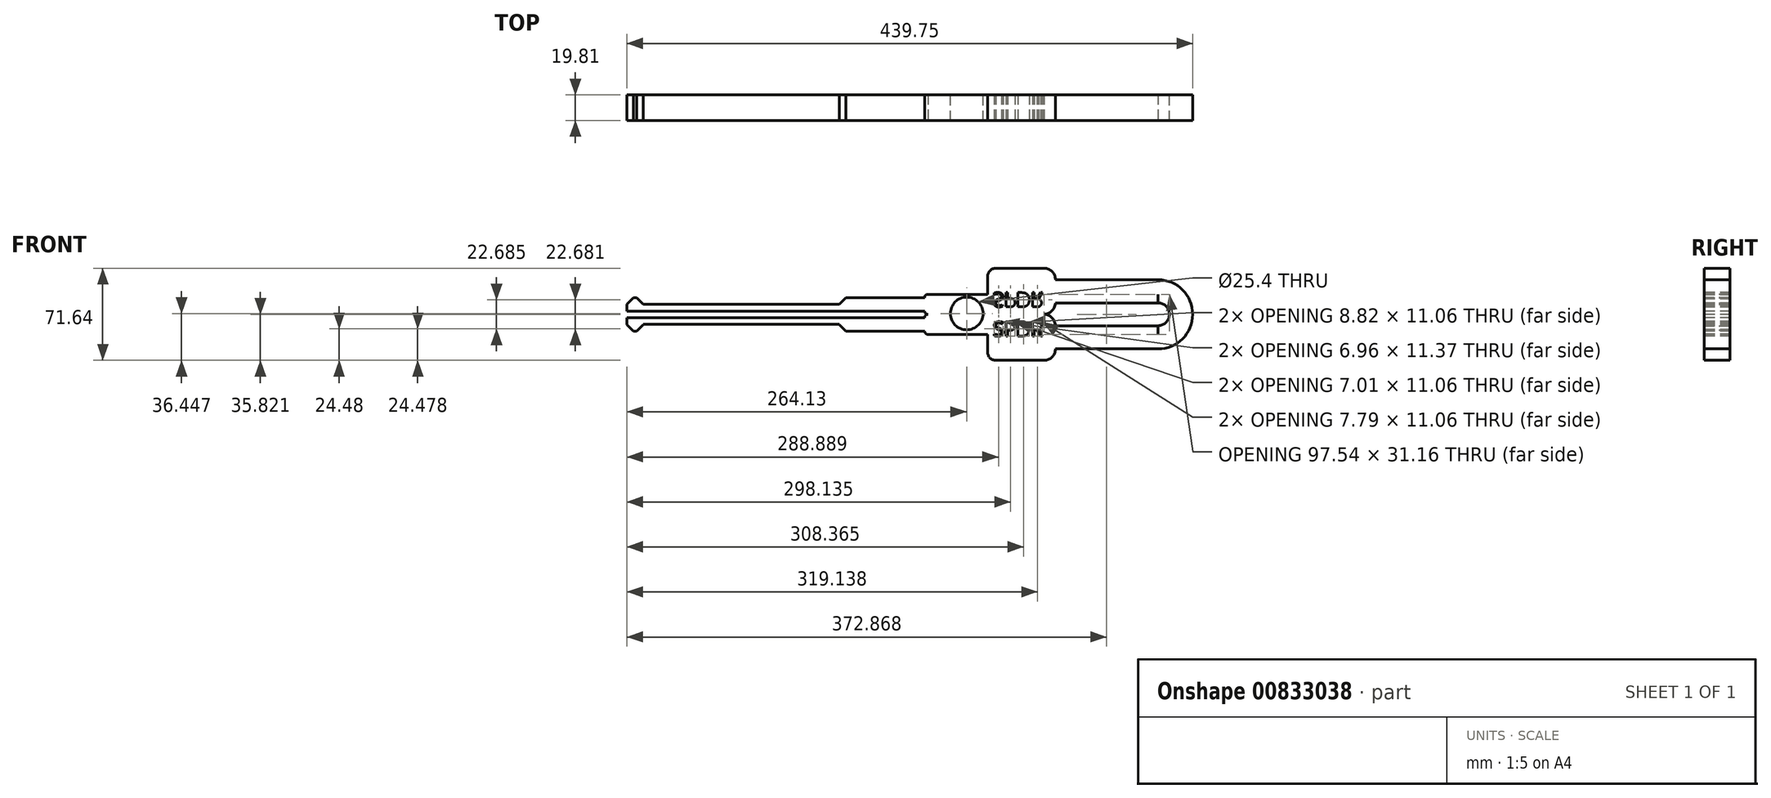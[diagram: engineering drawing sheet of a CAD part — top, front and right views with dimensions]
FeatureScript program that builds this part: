
annotation { "Feature Type Name" : "Feature", "Feature Type Description" : "" }
export const myFeature = defineFeature(function(context is Context, id is Id, definition is map)
    precondition{}
    {
        {
            var Q0;
            Q0=qCreatedBy(makeId("Front.planeOp"),FACE);
            var sketch = newSketch(context, id + "F0", { "sketchPlane" : qUnion([Q0])});
            skLineSegment(sketch, "E0.bottom", {"start": v(-48.26, 7.8) * mm, "end": v(41.91, 7.8) * mm});
            skLineSegment(sketch, "E0.top", {"start": v(-48.26, -7.8) * mm, "end": v(50.8, -7.8) * mm});
            skLineSegment(sketch, "E0.left", {"start": v(-50.8, 5.25) * mm, "end": v(-50.8, -5.25) * mm});
            skLineSegment(sketch, "E0.right", {"start": v(50.8, -1.1) * mm, "end": v(50.8, -7.8) * mm});
            skLineSegment(sketch, "E1.bottom", {"start": v(-1.8, -7.8) * mm, "end": v(50.88, -7.8) * mm});
            skLineSegment(sketch, "E1.top", {"start": v(4.55, -28.03) * mm, "end": v(42, -28.03) * mm});
            skLineSegment(sketch, "E1.left", {"start": v(-1.8, -7.8) * mm, "end": v(-1.8, -21.68) * mm});
            skLineSegment(sketch, "E1.right", {"start": v(50.88, -7.8) * mm, "end": v(50.88, -19.14) * mm});
            skPoint(sketch, "E2.visualSharp", {"position": v(-1.8, -28.03) * mm});
            skArc(sketch, "E2.filletArc", {"start": v(-1.8, -21.68) * mm, "mid": v(0.06, -26.17) * mm, "end": v(4.55, -28.03) * mm});
            skPoint(sketch, "E3.visualSharp", {"position": v(50.88, -28.03) * mm});
            skArc(sketch, "E3.filletArc", {"start": v(42, -28.03) * mm, "mid": v(48.28, -25.42) * mm, "end": v(50.88, -19.14) * mm});
            skPoint(sketch, "E4.visualSharp", {"position": v(50.8, 7.8) * mm});
            skArc(sketch, "E4.filletArc", {"start": v(50.8, -1.1) * mm, "mid": v(48.2, 5.19) * mm, "end": v(41.91, 7.8) * mm});
            skPoint(sketch, "E5.visualSharp", {"position": v(-50.8, -7.8) * mm});
            skArc(sketch, "E5.filletArc", {"start": v(-50.8, -5.25) * mm, "mid": v(-50.06, -7.05) * mm, "end": v(-48.26, -7.8) * mm});
            skPoint(sketch, "E6.visualSharp", {"position": v(-50.8, 7.8) * mm});
            skArc(sketch, "E6.filletArc", {"start": v(-48.26, 7.8) * mm, "mid": v(-50.06, 7.05) * mm, "end": v(-50.8, 5.25) * mm});
            skSolve(sketch);
        }
        {
            var Q0;
            Q0=makeQuery(id+"F0.imprint","IMPRINT",FACE,{"disambiguationData":[TD([[makeQuery(id+"F0.imprint","IMPRINT",EDGE,{"derivedFrom":sQuery(id+"F0.wireOp",EDGE,"E0.bottom")}),-1.0]])]});
            var Q1;
            Q1=makeQuery(id+"F0.imprint","IMPRINT",FACE,{"disambiguationData":[TD([[makeQuery(id+"F0.imprint","IMPRINT",EDGE,{"derivedFrom":sQuery(id+"F0.wireOp",EDGE,"E1.top")}),1.0]])]});
            extrude(context, id + "F1", {"entities" : qUnion([Q0, Q1]), "oppositeDirection" : true, "depth" : 19.8 * mm, "offsetDistance" : 25.4 * mm});
        }
        {
            var Q0;
            Q0=makeQuery(id+"F1.opExtrude","CAP_FACE",FACE,{"disambiguationData":[OSD([sQuery(id+"F0.wireOp",EDGE,"E0.bottom"),sQuery(id+"F0.wireOp",EDGE,"E0.top"),sQuery(id+"F0.wireOp",EDGE,"E0.left"),sQuery(id+"F0.wireOp",EDGE,"E0.right"),sQuery(id+"F0.wireOp",EDGE,"E1.bottom"),sQuery(id+"F0.wireOp",EDGE,"E1.top"),sQuery(id+"F0.wireOp",EDGE,"E1.left"),sQuery(id+"F0.wireOp",EDGE,"E1.right"),sQuery(id+"F0.wireOp",EDGE,"E2.filletArc"),sQuery(id+"F0.wireOp",EDGE,"E3.filletArc"),sQuery(id+"F0.wireOp",EDGE,"E4.filletArc"),sQuery(id+"F0.wireOp",EDGE,"E5.filletArc"),sQuery(id+"F0.wireOp",EDGE,"E6.filletArc")])],"isStart":true});
            var sketch = newSketch(context, id + "F2", { "sketchPlane" : qUnion([Q0])});
            skText(sketch, "E7", { "text": "SPDR", "fontName": "OpenSans-Regular.ttf"});
            const initialGuessF2  = {"E7": [0.00242, -0.00908, 1, 0, 0.01115]};
            skSetInitialGuess(sketch, initialGuessF2);
            skSolve(sketch);
        }
        {
            var Q0;
            Q0=makeQuery(id+"F2.imprint","IMPRINT",FACE,{"disambiguationData":[TD([[makeQuery(id+"F2.imprint","IMPRINT",EDGE,{"derivedFrom":sQuery(id+"F2.wireOp",EDGE,"E7.sketch_text.stroke-54")}),-1.0]])]});
            var Q1;
            Q1=makeQuery(id+"F2.imprint","IMPRINT",FACE,{"disambiguationData":[TD([[makeQuery(id+"F2.imprint","IMPRINT",EDGE,{"derivedFrom":sQuery(id+"F2.wireOp",EDGE,"E7.sketch_text.stroke-65")}),1.0]])]});
            var Q2;
            Q2=makeQuery(id+"F2.imprint","IMPRINT",FACE,{"disambiguationData":[TD([[makeQuery(id+"F2.imprint","IMPRINT",EDGE,{"derivedFrom":sQuery(id+"F2.wireOp",EDGE,"E7.sketch_text.stroke-40")}),-1.0]])]});
            var Q3;
            Q3=makeQuery(id+"F2.imprint","IMPRINT",FACE,{"disambiguationData":[TD([[makeQuery(id+"F2.imprint","IMPRINT",EDGE,{"derivedFrom":sQuery(id+"F2.wireOp",EDGE,"E7.sketch_text.stroke-47")}),1.0]])]});
            var Q4;
            Q4=makeQuery(id+"F2.imprint","IMPRINT",FACE,{"disambiguationData":[TD([[makeQuery(id+"F2.imprint","IMPRINT",EDGE,{"derivedFrom":sQuery(id+"F2.wireOp",EDGE,"E7.sketch_text.stroke-33")}),1.0]])]});
            var Q5;
            Q5=makeQuery(id+"F2.imprint","IMPRINT",FACE,{"disambiguationData":[TD([[makeQuery(id+"F2.imprint","IMPRINT",EDGE,{"derivedFrom":sQuery(id+"F2.wireOp",EDGE,"E7.sketch_text.stroke-25")}),-1.0]])]});
            var Q6;
            Q6=makeQuery(id+"F2.imprint","IMPRINT",FACE,{"disambiguationData":[TD([[makeQuery(id+"F2.imprint","IMPRINT",EDGE,{"derivedFrom":sQuery(id+"F2.wireOp",EDGE,"E7.sketch_text.stroke-0")}),-1.0]])]});
            extrude(context, id + "F3", {"entities" : qUnion([Q0, Q1, Q2, Q3, Q4, Q5, Q6]), "operationType" : NewBodyOperationType.REMOVE, "endBound" : BoundingType.THROUGH_ALL, "oppositeDirection" : true, "depth" : 44.45 * mm, "offsetDistance" : 25.4 * mm});
        }
        {
            var Q0;
            Q0=makeQuery(id+"F1.opExtrude","SWEPT_BODY",BODY,{"disambiguationData":[OSD([sQuery(id+"F0.wireOp",EDGE,"E0.bottom"),sQuery(id+"F0.wireOp",EDGE,"E0.top"),sQuery(id+"F0.wireOp",EDGE,"E0.left"),sQuery(id+"F0.wireOp",EDGE,"E0.right"),sQuery(id+"F0.wireOp",EDGE,"E1.bottom"),sQuery(id+"F0.wireOp",EDGE,"E1.top"),sQuery(id+"F0.wireOp",EDGE,"E1.left"),sQuery(id+"F0.wireOp",EDGE,"E1.right"),sQuery(id+"F0.wireOp",EDGE,"E2.filletArc"),sQuery(id+"F0.wireOp",EDGE,"E3.filletArc"),sQuery(id+"F0.wireOp",EDGE,"E4.filletArc"),sQuery(id+"F0.wireOp",EDGE,"E5.filletArc"),sQuery(id+"F0.wireOp",EDGE,"E6.filletArc")])]});
            var Q1;
            Q1=makeQuery(id+"F1.opExtrude","SWEPT_FACE",FACE,{"disambiguationData":[OSD([sQuery(id+"F0.wireOp",EDGE,"E0.bottom")])]});
            mirror(context, id + "F4", {"operationType" : NewBodyOperationType.ADD, "entities" : qUnion([Q0]), "mirrorPlane" : qUnion([Q1])});
        }
        {
            var Q0;
            Q0=makeQuery(id+"F4.opPattern","COPY",FACE,{"derivedFrom":makeQuery(id+"F1.opExtrude","SWEPT_FACE",FACE,{"disambiguationData":[OSD([sQuery(id+"F0.wireOp",EDGE,"E0.left")])]}),"instanceName":"1"});
            var Q1;
            Q1=makeQuery(id+"F1.opExtrude","SWEPT_FACE",FACE,{"disambiguationData":[OSD([sQuery(id+"F0.wireOp",EDGE,"E0.left")])]});
            extrude(context, id + "F5", {"entities" : qUnion([Q0, Q1]), "operationType" : NewBodyOperationType.ADD, "depth" : 231.4 * mm, "offsetDistance" : 25.4 * mm});
        }
        {
            var Q0;
            {var subQ0=sQuery(id+"F0.wireOp",EDGE,"E0.left");var subQ1=makeQuery(id+"F1.opExtrude","CAP_EDGE",EDGE,{"disambiguationData":[OSD([subQ0])],"isStart":true});var subQ2=makeQuery(id+"F1.opExtrude","CAP_FACE",FACE,{"disambiguationData":[OSD([sQuery(id+"F0.wireOp",EDGE,"E0.bottom"),sQuery(id+"F0.wireOp",EDGE,"E0.top"),subQ0,sQuery(id+"F0.wireOp",EDGE,"E0.right"),sQuery(id+"F0.wireOp",EDGE,"E1.bottom"),sQuery(id+"F0.wireOp",EDGE,"E1.top"),sQuery(id+"F0.wireOp",EDGE,"E1.left"),sQuery(id+"F0.wireOp",EDGE,"E1.right"),sQuery(id+"F0.wireOp",EDGE,"E2.filletArc"),sQuery(id+"F0.wireOp",EDGE,"E3.filletArc"),sQuery(id+"F0.wireOp",EDGE,"E4.filletArc"),sQuery(id+"F0.wireOp",EDGE,"E5.filletArc"),sQuery(id+"F0.wireOp",EDGE,"E6.filletArc")])],"isStart":true});Q0=makeQuery(id+"F5.boolean.opBoolean","MERGE",FACE,{"derivedFrom":[makeQuery(id+"F4.boolean.opBoolean","MERGE",FACE,{"derivedFrom":[subQ2,makeQuery(id+"F4.opPattern","COPY",FACE,{"derivedFrom":subQ2,"instanceName":"1"})]}),makeQuery(id+"F5.opExtrude","SWEPT_FACE",FACE,{"disambiguationData":[OSD([subQ0]),TDD([subQ1])]}),makeQuery(id+"F5.opExtrude","SWEPT_FACE",FACE,{"disambiguationData":[OSD([subQ0]),TDD([makeQuery(id+"F4.opPattern","COPY",EDGE,{"derivedFrom":subQ1,"instanceName":"1"})])]})]});}
            var sketch = newSketch(context, id + "F6", { "sketchPlane" : qUnion([Q0])});
            skLineSegment(sketch, "E8.bottom", {"start": v(-117.1, -10.5) * mm, "end": v(-269.5, -10.5) * mm});
            skLineSegment(sketch, "E8.top", {"start": v(-117.1, 0) * mm, "end": v(-269.5, 0) * mm});
            skLineSegment(sketch, "E8.left", {"start": v(-117.1, -10.5) * mm, "end": v(-117.1, 0) * mm});
            skLineSegment(sketch, "E8.right", {"start": v(-269.5, -10.5) * mm, "end": v(-269.5, 0) * mm});
            skLineSegment(sketch, "E9.bottom", {"start": v(-117.1, 15.58) * mm, "end": v(-269.5, 15.58) * mm});
            skLineSegment(sketch, "E9.top", {"start": v(-117.1, 26.08) * mm, "end": v(-269.5, 26.08) * mm});
            skLineSegment(sketch, "E9.left", {"start": v(-117.1, 15.58) * mm, "end": v(-117.1, 26.08) * mm});
            skLineSegment(sketch, "E9.right", {"start": v(-269.5, 15.58) * mm, "end": v(-269.5, 26.08) * mm});
            skPoint(sketch, "E10", {"position": v(-282.2, 0) * mm});
            skSolve(sketch);
        }
        {
            var Q0;
            {var subQ0=sQuery(id+"F6.wireOp",EDGE,"E8.bottom");Q0=makeQuery(id+"F6.imprint","IMPRINT",FACE,{"disambiguationData":[TD([[makeQuery(id+"F6.imprint","IMPRINT",EDGE,{"derivedFrom":subQ0}),-1.0]])]});}
            var Q1;
            {var subQ0=sQuery(id+"F6.wireOp",EDGE,"E8.top");Q1=makeQuery(id+"F6.imprint","IMPRINT",FACE,{"disambiguationData":[TD([[makeQuery(id+"F6.imprint","IMPRINT",EDGE,{"derivedFrom":subQ0}),1.0]])]});}
            var Q2;
            {var subQ0=sQuery(id+"F6.wireOp",EDGE,"E9.top");Q2=makeQuery(id+"F6.imprint","IMPRINT",FACE,{"disambiguationData":[TD([[makeQuery(id+"F6.imprint","IMPRINT",EDGE,{"derivedFrom":subQ0}),1.0]])]});}
            var Q3;
            {var subQ0=sQuery(id+"F6.wireOp",EDGE,"E9.bottom");Q3=makeQuery(id+"F6.imprint","IMPRINT",FACE,{"disambiguationData":[TD([[makeQuery(id+"F6.imprint","IMPRINT",EDGE,{"derivedFrom":subQ0}),-1.0]])]});}
            extrude(context, id + "F7", {"entities" : qUnion([Q0, Q1, Q2, Q3]), "operationType" : NewBodyOperationType.REMOVE, "oppositeDirection" : true, "depth" : 25.4 * mm, "offsetDistance" : 25.4 * mm});
        }
        {
            var Q0;
            {var subQ0=sQuery(id+"F0.wireOp",EDGE,"E0.left");var subQ1=makeQuery(id+"F1.opExtrude","CAP_EDGE",EDGE,{"disambiguationData":[OSD([subQ0])],"isStart":false});var subQ2=makeQuery(id+"F1.opExtrude","CAP_FACE",FACE,{"disambiguationData":[OSD([sQuery(id+"F0.wireOp",EDGE,"E0.bottom"),sQuery(id+"F0.wireOp",EDGE,"E0.top"),subQ0,sQuery(id+"F0.wireOp",EDGE,"E0.right"),sQuery(id+"F0.wireOp",EDGE,"E1.bottom"),sQuery(id+"F0.wireOp",EDGE,"E1.top"),sQuery(id+"F0.wireOp",EDGE,"E1.left"),sQuery(id+"F0.wireOp",EDGE,"E1.right"),sQuery(id+"F0.wireOp",EDGE,"E2.filletArc"),sQuery(id+"F0.wireOp",EDGE,"E3.filletArc"),sQuery(id+"F0.wireOp",EDGE,"E4.filletArc"),sQuery(id+"F0.wireOp",EDGE,"E5.filletArc"),sQuery(id+"F0.wireOp",EDGE,"E6.filletArc")])],"isStart":false});Q0=makeQuery(id+"F5.boolean.opBoolean","MERGE",FACE,{"derivedFrom":[makeQuery(id+"F4.boolean.opBoolean","MERGE",FACE,{"derivedFrom":[subQ2,makeQuery(id+"F4.opPattern","COPY",FACE,{"derivedFrom":subQ2,"instanceName":"1"})]}),makeQuery(id+"F5.opExtrude","SWEPT_FACE",FACE,{"disambiguationData":[OSD([subQ0]),TDD([subQ1])]}),makeQuery(id+"F5.opExtrude","SWEPT_FACE",FACE,{"disambiguationData":[OSD([subQ0]),TDD([makeQuery(id+"F4.opPattern","COPY",EDGE,{"derivedFrom":subQ1,"instanceName":"1"})])]})]});}
            var sketch = newSketch(context, id + "F8", { "sketchPlane" : qUnion([Q0])});
            skCircle(sketch, "E11", {"center": v(18.06, 8.42) * mm, "radius": 12.7 * mm});
            skSolve(sketch);
        }
        {
            var Q0;
            Q0 = qSketchRegion(id + "F8", true);
            extrude(context, id + "F9", {"entities" : qUnion([Q0]), "operationType" : NewBodyOperationType.REMOVE, "oppositeDirection" : true, "depth" : 93.47 * mm, "offsetDistance" : 25.4 * mm});
        }
        {
            var Q0;
            {var subQ0=sQuery(id+"F0.wireOp",EDGE,"E5.filletArc");var subQ1=sQuery(id+"F0.wireOp",EDGE,"E0.left");Q0=makeQuery(id+"F7.boolean.opBoolean","INTERSECT",EDGE,{"derivedFrom":[makeQuery(id+"F5.opExtrude","SWEPT_FACE",FACE,{"disambiguationData":[OSD([subQ1,subQ0]),TDD([makeQuery(id+"F4.opPattern","COPY",EDGE,{"derivedFrom":makeQuery(id+"F1.opExtrude","SWEPT_EDGE",EDGE,{"disambiguationData":[OSD([subQ1,subQ0])]}),"instanceName":"1"})])]}),makeQuery(id+"F7.opExtrude","SWEPT_FACE",FACE,{"disambiguationData":[OSD([sQuery(id+"F6.wireOp",EDGE,"E9.left")])]})]});}
            var Q1;
            {var subQ0=sQuery(id+"F0.wireOp",EDGE,"E5.filletArc");var subQ1=sQuery(id+"F0.wireOp",EDGE,"E0.left");Q1=makeQuery(id+"F7.boolean.opBoolean","INTERSECT",EDGE,{"derivedFrom":[makeQuery(id+"F5.opExtrude","SWEPT_FACE",FACE,{"disambiguationData":[OSD([subQ1,subQ0]),TDD([makeQuery(id+"F4.opPattern","COPY",EDGE,{"derivedFrom":makeQuery(id+"F1.opExtrude","SWEPT_EDGE",EDGE,{"disambiguationData":[OSD([subQ1,subQ0])]}),"instanceName":"1"})])]}),makeQuery(id+"F7.opExtrude","SWEPT_FACE",FACE,{"disambiguationData":[OSD([sQuery(id+"F6.wireOp",EDGE,"E9.right")])]})]});}
            var Q2;
            {var subQ0=sQuery(id+"F0.wireOp",EDGE,"E5.filletArc");var subQ1=sQuery(id+"F0.wireOp",EDGE,"E0.left");Q2=makeQuery(id+"F7.boolean.opBoolean","INTERSECT",EDGE,{"derivedFrom":[makeQuery(id+"F5.opExtrude","SWEPT_FACE",FACE,{"disambiguationData":[OSD([subQ1,subQ0]),TDD([makeQuery(id+"F1.opExtrude","SWEPT_EDGE",EDGE,{"disambiguationData":[OSD([subQ1,subQ0])]})])]}),makeQuery(id+"F7.opExtrude","SWEPT_FACE",FACE,{"disambiguationData":[OSD([sQuery(id+"F6.wireOp",EDGE,"E8.left")])]})]});}
            var Q3;
            {var subQ0=sQuery(id+"F0.wireOp",EDGE,"E5.filletArc");var subQ1=sQuery(id+"F0.wireOp",EDGE,"E0.left");Q3=makeQuery(id+"F7.boolean.opBoolean","INTERSECT",EDGE,{"derivedFrom":[makeQuery(id+"F5.opExtrude","SWEPT_FACE",FACE,{"disambiguationData":[OSD([subQ1,subQ0]),TDD([makeQuery(id+"F1.opExtrude","SWEPT_EDGE",EDGE,{"disambiguationData":[OSD([subQ1,subQ0])]})])]}),makeQuery(id+"F7.opExtrude","SWEPT_FACE",FACE,{"disambiguationData":[OSD([sQuery(id+"F6.wireOp",EDGE,"E8.right")])]})]});}
            var Q4;
            {var subQ0=sQuery(id+"F0.wireOp",EDGE,"E5.filletArc");var subQ1=sQuery(id+"F0.wireOp",EDGE,"E0.left");Q4=makeQuery(id+"F5.opExtrude","CAP_EDGE",EDGE,{"disambiguationData":[OSD([subQ1,subQ0]),TDD([makeQuery(id+"F1.opExtrude","SWEPT_EDGE",EDGE,{"disambiguationData":[OSD([subQ1,subQ0])]})])],"isStart":false});}
            var Q5;
            {var subQ0=sQuery(id+"F0.wireOp",EDGE,"E5.filletArc");var subQ1=sQuery(id+"F0.wireOp",EDGE,"E0.left");Q5=makeQuery(id+"F5.opExtrude","CAP_EDGE",EDGE,{"disambiguationData":[OSD([subQ1,subQ0]),TDD([makeQuery(id+"F4.opPattern","COPY",EDGE,{"derivedFrom":makeQuery(id+"F1.opExtrude","SWEPT_EDGE",EDGE,{"disambiguationData":[OSD([subQ1,subQ0])]}),"instanceName":"1"})])],"isStart":false});}
            chamfer(context, id + "F10", {"entities" : qUnion([Q0, Q1, Q2, Q3, Q4, Q5]), "width" : 5.08 * mm, "tangentPropagation" : true});
        }
        {
            var Q0;
            Q0=makeQuery(id+"F4.opPattern","COPY",FACE,{"derivedFrom":makeQuery(id+"F1.opExtrude","SWEPT_FACE",FACE,{"disambiguationData":[OSD([sQuery(id+"F0.wireOp",EDGE,"E1.right")])]}),"instanceName":"1"});
            var Q1;
            Q1=makeQuery(id+"F4.opPattern","COPY",FACE,{"derivedFrom":makeQuery(id+"F1.opExtrude","SWEPT_FACE",FACE,{"disambiguationData":[OSD([sQuery(id+"F0.wireOp",EDGE,"E0.right")])]}),"instanceName":"1"});
            var Q2;
            Q2=makeQuery(id+"F1.opExtrude","SWEPT_FACE",FACE,{"disambiguationData":[OSD([sQuery(id+"F0.wireOp",EDGE,"E0.right")])]});
            var Q3;
            Q3=makeQuery(id+"F1.opExtrude","SWEPT_FACE",FACE,{"disambiguationData":[OSD([sQuery(id+"F0.wireOp",EDGE,"E1.right")])]});
            extrude(context, id + "F11", {"entities" : qUnion([Q0, Q1, Q2, Q3]), "operationType" : NewBodyOperationType.ADD, "depth" : 79.76 * mm, "offsetDistance" : 25.4 * mm});
        }
        {
            var Q0;
            {var subQ0=sQuery(id+"F0.wireOp",EDGE,"E1.right");var subQ1=makeQuery(id+"F1.opExtrude","CAP_EDGE",EDGE,{"disambiguationData":[OSD([subQ0])],"isStart":false});var subQ2=sQuery(id+"F0.wireOp",EDGE,"E0.right");var subQ3=makeQuery(id+"F1.opExtrude","CAP_EDGE",EDGE,{"disambiguationData":[OSD([subQ2])],"isStart":false});var subQ4=sQuery(id+"F0.wireOp",EDGE,"E0.left");var subQ5=makeQuery(id+"F1.opExtrude","CAP_EDGE",EDGE,{"disambiguationData":[OSD([subQ4])],"isStart":false});var subQ6=makeQuery(id+"F1.opExtrude","CAP_FACE",FACE,{"disambiguationData":[OSD([sQuery(id+"F0.wireOp",EDGE,"E0.bottom"),sQuery(id+"F0.wireOp",EDGE,"E0.top"),subQ4,subQ2,sQuery(id+"F0.wireOp",EDGE,"E1.bottom"),sQuery(id+"F0.wireOp",EDGE,"E1.top"),sQuery(id+"F0.wireOp",EDGE,"E1.left"),subQ0,sQuery(id+"F0.wireOp",EDGE,"E2.filletArc"),sQuery(id+"F0.wireOp",EDGE,"E3.filletArc"),sQuery(id+"F0.wireOp",EDGE,"E4.filletArc"),sQuery(id+"F0.wireOp",EDGE,"E5.filletArc"),sQuery(id+"F0.wireOp",EDGE,"E6.filletArc")])],"isStart":false});Q0=makeQuery(id+"F11.boolean.opBoolean","MERGE",FACE,{"derivedFrom":[makeQuery(id+"F5.boolean.opBoolean","MERGE",FACE,{"derivedFrom":[makeQuery(id+"F4.boolean.opBoolean","MERGE",FACE,{"derivedFrom":[subQ6,makeQuery(id+"F4.opPattern","COPY",FACE,{"derivedFrom":subQ6,"instanceName":"1"})]}),makeQuery(id+"F5.opExtrude","SWEPT_FACE",FACE,{"disambiguationData":[OSD([subQ4]),TDD([subQ5])]}),makeQuery(id+"F5.opExtrude","SWEPT_FACE",FACE,{"disambiguationData":[OSD([subQ4]),TDD([makeQuery(id+"F4.opPattern","COPY",EDGE,{"derivedFrom":subQ5,"instanceName":"1"})])]})]}),makeQuery(id+"F11.opExtrude","SWEPT_FACE",FACE,{"disambiguationData":[OSD([subQ2]),TDD([subQ3])]}),makeQuery(id+"F11.opExtrude","SWEPT_FACE",FACE,{"disambiguationData":[OSD([subQ0]),TDD([subQ1])]}),makeQuery(id+"F11.opExtrude","SWEPT_FACE",FACE,{"disambiguationData":[OSD([subQ2]),TDD([makeQuery(id+"F4.opPattern","COPY",EDGE,{"derivedFrom":subQ3,"instanceName":"1"})])]}),makeQuery(id+"F11.opExtrude","SWEPT_FACE",FACE,{"disambiguationData":[OSD([subQ0]),TDD([makeQuery(id+"F4.opPattern","COPY",EDGE,{"derivedFrom":subQ1,"instanceName":"1"})])]})]});}
            var sketch = newSketch(context, id + "F12", { "sketchPlane" : qUnion([Q0])});
            skArc(sketch, "E12", {"start": v(-130.64, 34.72) * mm, "mid": v(-157.56, 7.8) * mm, "end": v(-130.64, -19.14) * mm});
            skLineSegment(sketch, "E13", {"start": v(-130.64, -19.14) * mm, "end": v(-130.64, -1.1) * mm});
            skArc(sketch, "E14", {"start": v(-130.56, 16.68) * mm, "mid": v(-139.45, 7.8) * mm, "end": v(-130.56, -1.1) * mm});
            skLineSegment(sketch, "E15.trimOffspring", {"start": v(-130.64, 16.68) * mm, "end": v(-130.64, 34.72) * mm});
            skSolve(sketch);
        }
        {
            var Q0;
            {var subQ9=sQuery(id+"F12.wireOp",EDGE,"E12");Q0=makeQuery(id+"F12.imprint","IMPRINT",FACE,{"disambiguationData":[TD([[makeQuery(id+"F12.imprint","IMPRINT",EDGE,{"derivedFrom":subQ9}),1.0]])]});}
            var Q1;
            {var subQ0=sQuery(id+"F0.wireOp",EDGE,"E1.right");var subQ1=makeQuery(id+"F1.opExtrude","CAP_EDGE",EDGE,{"disambiguationData":[OSD([subQ0])],"isStart":true});var subQ2=sQuery(id+"F0.wireOp",EDGE,"E0.right");var subQ3=makeQuery(id+"F1.opExtrude","CAP_EDGE",EDGE,{"disambiguationData":[OSD([subQ2])],"isStart":true});var subQ4=sQuery(id+"F0.wireOp",EDGE,"E0.left");var subQ5=makeQuery(id+"F1.opExtrude","CAP_EDGE",EDGE,{"disambiguationData":[OSD([subQ4])],"isStart":true});var subQ6=makeQuery(id+"F1.opExtrude","CAP_FACE",FACE,{"disambiguationData":[OSD([sQuery(id+"F0.wireOp",EDGE,"E0.bottom"),sQuery(id+"F0.wireOp",EDGE,"E0.top"),subQ4,subQ2,sQuery(id+"F0.wireOp",EDGE,"E1.bottom"),sQuery(id+"F0.wireOp",EDGE,"E1.top"),sQuery(id+"F0.wireOp",EDGE,"E1.left"),subQ0,sQuery(id+"F0.wireOp",EDGE,"E2.filletArc"),sQuery(id+"F0.wireOp",EDGE,"E3.filletArc"),sQuery(id+"F0.wireOp",EDGE,"E4.filletArc"),sQuery(id+"F0.wireOp",EDGE,"E5.filletArc"),sQuery(id+"F0.wireOp",EDGE,"E6.filletArc")])],"isStart":true});Q1=makeQuery(id+"F11.boolean.opBoolean","MERGE",FACE,{"derivedFrom":[makeQuery(id+"F5.boolean.opBoolean","MERGE",FACE,{"derivedFrom":[makeQuery(id+"F4.boolean.opBoolean","MERGE",FACE,{"derivedFrom":[subQ6,makeQuery(id+"F4.opPattern","COPY",FACE,{"derivedFrom":subQ6,"instanceName":"1"})]}),makeQuery(id+"F5.opExtrude","SWEPT_FACE",FACE,{"disambiguationData":[OSD([subQ4]),TDD([subQ5])]}),makeQuery(id+"F5.opExtrude","SWEPT_FACE",FACE,{"disambiguationData":[OSD([subQ4]),TDD([makeQuery(id+"F4.opPattern","COPY",EDGE,{"derivedFrom":subQ5,"instanceName":"1"})])]})]}),makeQuery(id+"F11.opExtrude","SWEPT_FACE",FACE,{"disambiguationData":[OSD([subQ2]),TDD([subQ3])]}),makeQuery(id+"F11.opExtrude","SWEPT_FACE",FACE,{"disambiguationData":[OSD([subQ0]),TDD([subQ1])]}),makeQuery(id+"F11.opExtrude","SWEPT_FACE",FACE,{"disambiguationData":[OSD([subQ2]),TDD([makeQuery(id+"F4.opPattern","COPY",EDGE,{"derivedFrom":subQ3,"instanceName":"1"})])]}),makeQuery(id+"F11.opExtrude","SWEPT_FACE",FACE,{"disambiguationData":[OSD([subQ0]),TDD([makeQuery(id+"F4.opPattern","COPY",EDGE,{"derivedFrom":subQ1,"instanceName":"1"})])]})]});}
            extrude(context, id + "F13", {"entities" : qUnion([Q0]), "operationType" : NewBodyOperationType.ADD, "endBound" : BoundingType.UP_TO_SURFACE, "oppositeDirection" : true, "depth" : 25.4 * mm, "endBoundEntityFace" : qUnion([Q1]), "offsetDistance" : 25.4 * mm});
        }
    });
